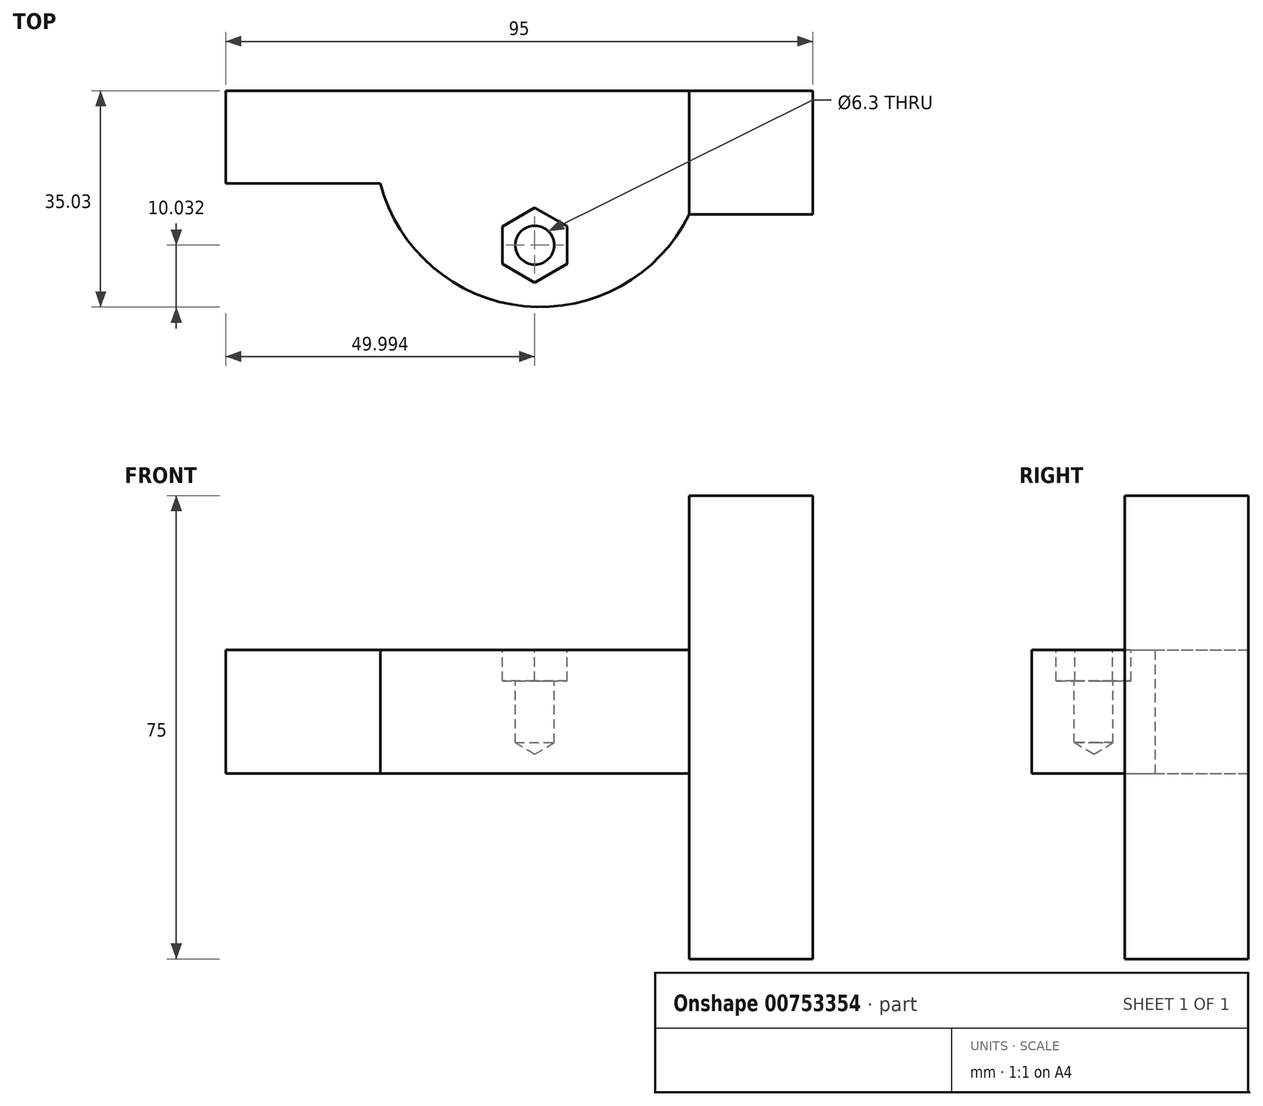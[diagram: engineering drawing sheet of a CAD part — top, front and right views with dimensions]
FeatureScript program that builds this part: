
annotation { "Feature Type Name" : "Feature", "Feature Type Description" : "" }
export const myFeature = defineFeature(function(context is Context, id is Id, definition is map)
    precondition{}
    {
        {
            var Q0;
            Q0=qCreatedBy(makeId("Front.planeOp"),FACE);
            var sketch = newSketch(context, id + "F0", { "sketchPlane" : qUnion([Q0])});
            skLineSegment(sketch, "E0", {"start": v(-45, 35) * mm, "end": v(-45, -40) * mm});
            skLineSegment(sketch, "E1", {"start": v(-45, -40) * mm, "end": v(-25, -40) * mm});
            skLineSegment(sketch, "E2", {"start": v(-25, -40) * mm, "end": v(-25, -10) * mm});
            skLineSegment(sketch, "E3", {"start": v(50, -10) * mm, "end": v(50, 10) * mm});
            skLineSegment(sketch, "E4", {"start": v(50, 10) * mm, "end": v(-25, 10) * mm});
            skLineSegment(sketch, "E5", {"start": v(-25, 10) * mm, "end": v(-25, 35) * mm});
            skLineSegment(sketch, "E6", {"start": v(-25, 35) * mm, "end": v(-45, 35) * mm});
            skLineSegment(sketch, "E7", {"start": v(50, -10) * mm, "end": v(-25, -10) * mm});
            skLineSegment(sketch, "E8", {"start": v(-25, 10) * mm, "end": v(-25, -10) * mm});
            skSolve(sketch);
        }
        {
            var Q0;
            Q0=makeQuery(id+"F0.imprint","IMPRINT",FACE,{"disambiguationData":[TD([[makeQuery(id+"F0.imprint","IMPRINT",EDGE,{"derivedFrom":sQuery(id+"F0.wireOp",EDGE,"E0")}),1.0]])]});
            extrude(context, id + "F1", {"entities" : qUnion([Q0]), "depth" : 20 * mm, "offsetDistance" : 25 * mm});
        }
        {
            var Q0;
            Q0=makeQuery(id+"F0.imprint","IMPRINT",FACE,{"disambiguationData":[TD([[makeQuery(id+"F0.imprint","IMPRINT",EDGE,{"derivedFrom":sQuery(id+"F0.wireOp",EDGE,"E3")}),1.0]])]});
            extrude(context, id + "F2", {"entities" : qUnion([Q0]), "operationType" : NewBodyOperationType.ADD, "depth" : 15 * mm, "offsetDistance" : 25 * mm});
        }
        {
            var Q0;
            Q0=qCreatedBy(makeId("Top.planeOp"),FACE);
            var sketch = newSketch(context, id + "F3", { "sketchPlane" : qUnion([Q0])});
            skLineSegment(sketch, "E9", {"start": v(0, -25) * mm, "end": v(0, 0) * mm});
            skPoint(sketch, "E10", {"position": v(-25, -20) * mm});
            skPoint(sketch, "E11", {"position": v(25, -15) * mm});
            skArc(sketch, "E12", {"start": v(-25, -20) * mm, "mid": v(1.74, -34.9) * mm, "end": v(25, -15) * mm});
            skLineSegment(sketch, "E13", {"start": v(-25, -20) * mm, "end": v(-25, -15) * mm});
            skLineSegment(sketch, "E14", {"start": v(-25, -15) * mm, "end": v(25, -15) * mm});
            skSolve(sketch);
        }
        {
            var Q0;
            {var subQ0=sQuery(id+"F3.wireOp",EDGE,"E12");Q0=makeQuery(id+"F3.imprint","IMPRINT",FACE,{"disambiguationData":[TD([[makeQuery(id+"F3.imprint","IMPRINT",EDGE,{"derivedFrom":subQ0}),1.0]])]});}
            extrude(context, id + "F4", {"entities" : qUnion([Q0]), "operationType" : NewBodyOperationType.ADD, "endBound" : BoundingType.SYMMETRIC, "depth" : 20 * mm, "offsetDistance" : 25 * mm});
        }
        {
            var Q0;
            Q0=makeQuery(id+"F4.boolean.opBoolean","MERGE",FACE,{"derivedFrom":[makeQuery(id+"F2.opExtrude","SWEPT_FACE",FACE,{"disambiguationData":[OSD([sQuery(id+"F0.wireOp",EDGE,"E4")])]}),makeQuery(id+"F4.opExtrude","CAP_FACE",FACE,{"disambiguationData":[OSD([sQuery(id+"F3.wireOp",EDGE,"E12"),sQuery(id+"F3.wireOp",EDGE,"E13"),sQuery(id+"F3.wireOp",EDGE,"E14")])],"isStart":false})]});
            var sketch = newSketch(context, id + "F5", { "sketchPlane" : qUnion([Q0])});
            skCircle(sketch, "E15.cCircle", {"center": v(0, -25) * mm, "radius": 5.25 * mm, "construction": true});
            skLineSegment(sketch, "E15.0", {"start": v(0, -18.94) * mm, "end": v(5.26, -21.97) * mm});
            skLineSegment(sketch, "E15.1", {"start": v(5.26, -21.97) * mm, "end": v(5.25, -28.03) * mm});
            skLineSegment(sketch, "E15.2", {"start": v(5.25, -28.03) * mm, "end": v(0, -31.06) * mm});
            skLineSegment(sketch, "E15.3", {"start": v(0, -31.06) * mm, "end": v(-5.25, -28.03) * mm});
            skLineSegment(sketch, "E15.4", {"start": v(-5.25, -28.03) * mm, "end": v(-5.24, -21.96) * mm});
            skLineSegment(sketch, "E15.5", {"start": v(-5.24, -21.96) * mm, "end": v(0, -18.94) * mm});
            skPoint(sketch, "E15.0.midPoint", {"position": v(2.63, -20.45) * mm});
            skSolve(sketch);
        }
        {
            var Q0;
            Q0=makeQuery(id+"F5.imprint","IMPRINT",FACE,{"disambiguationData":[TD([[makeQuery(id+"F5.imprint","IMPRINT",EDGE,{"derivedFrom":sQuery(id+"F5.wireOp",EDGE,"E15.0")}),-1.0]])]});
            extrude(context, id + "F6", {"entities" : qUnion([Q0]), "operationType" : NewBodyOperationType.REMOVE, "oppositeDirection" : true, "depth" : 5 * mm, "offsetDistance" : 25 * mm});
        }
        {
            var Q0;
            Q0=sQuery(id+"F5.wireOp",VERTEX,"E15.cCircle.center");
            var Q1;
            Q1=makeQuery(id+"F1.opExtrude","SWEPT_BODY",BODY,{"disambiguationData":[OSD([sQuery(id+"F0.wireOp",EDGE,"E0"),sQuery(id+"F0.wireOp",EDGE,"E1"),sQuery(id+"F0.wireOp",EDGE,"E2"),sQuery(id+"F0.wireOp",EDGE,"E5"),sQuery(id+"F0.wireOp",EDGE,"E6"),sQuery(id+"F0.wireOp",EDGE,"E8")])]});
            hole(context, id + "F7", {"style" : HoleStyle.SIMPLE, "endStyle" : HoleEndStyle.BLIND, "standardTappedOrClearance" : lookupTablePath({ "fit" : "Close", "standard" : "ISO", "size" : "M6", "type" : "Clearance" }), "standardBlindInLast" : lookupTablePath({ "fit" : "Close", "standard" : "ISO", "size" : "M6", "type" : "Clearance" }), "holeDiameter" : 6.3 * mm, "majorDiameter" : 5 * mm, "holeDepth" : 15 * mm, "isTappedThrough" : true, "tappedDepth" : 12 * mm, "tapClearance" : 3, "startFromSketch" : true, "locations" : qUnion([Q0]), "scope" : qUnion([Q1])});
        }
        {
            var Q0;
            Q0=makeQuery(id+"F1.opExtrude","SWEPT_BODY",BODY,{"disambiguationData":[OSD([sQuery(id+"F0.wireOp",EDGE,"E0"),sQuery(id+"F0.wireOp",EDGE,"E1"),sQuery(id+"F0.wireOp",EDGE,"E2"),sQuery(id+"F0.wireOp",EDGE,"E5"),sQuery(id+"F0.wireOp",EDGE,"E6"),sQuery(id+"F0.wireOp",EDGE,"E8")])]});
            var Q1;
            Q1=makeQuery(id+"F2.opExtrude","SWEPT_FACE",FACE,{"disambiguationData":[OSD([sQuery(id+"F0.wireOp",EDGE,"E3")])]});
            mirror(context, id + "F8", {"entities" : qUnion([Q0]), "mirrorPlane" : qUnion([Q1])});
        }
        {
            var Q0;
            Q0=makeQuery(id+"F1.opExtrude","SWEPT_BODY",BODY,{"disambiguationData":[OSD([sQuery(id+"F0.wireOp",EDGE,"E0"),sQuery(id+"F0.wireOp",EDGE,"E1"),sQuery(id+"F0.wireOp",EDGE,"E2"),sQuery(id+"F0.wireOp",EDGE,"E5"),sQuery(id+"F0.wireOp",EDGE,"E6"),sQuery(id+"F0.wireOp",EDGE,"E8")])]});
            deleteBodies(context, id + "F9", {"entities" : qUnion([Q0])});
        }
    });
